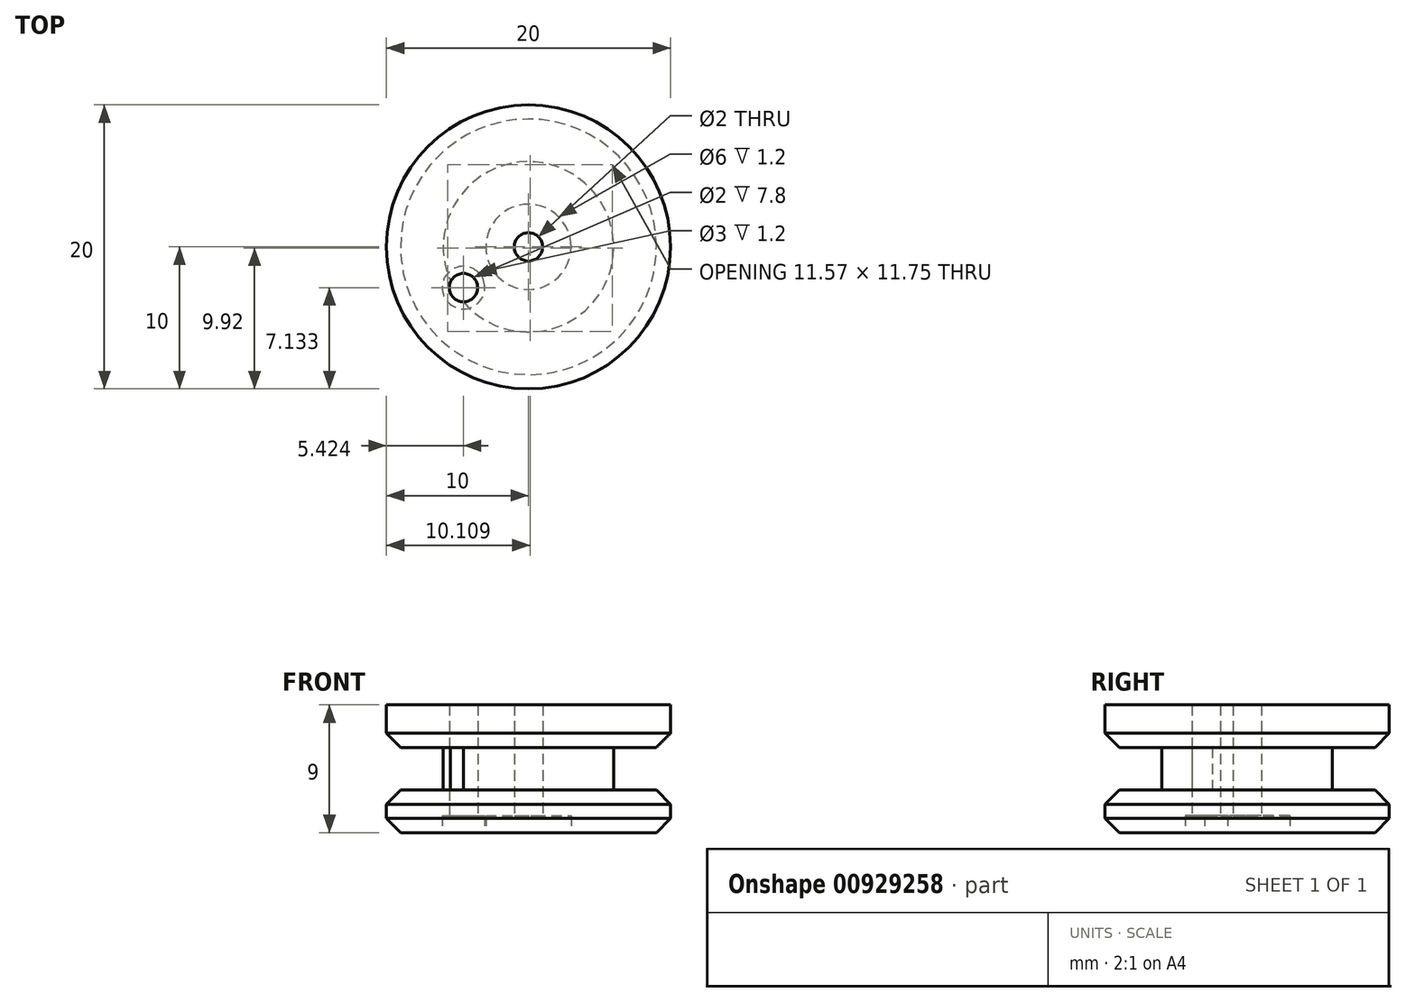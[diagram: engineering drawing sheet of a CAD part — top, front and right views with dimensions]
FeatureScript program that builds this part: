
annotation { "Feature Type Name" : "Feature", "Feature Type Description" : "" }
export const myFeature = defineFeature(function(context is Context, id is Id, definition is map)
    precondition{}
    {
        {
            var Q0;
            Q0=qCreatedBy(makeId("Top.planeOp"),FACE);
            var sketch = newSketch(context, id + "F0", { "sketchPlane" : qUnion([Q0])});
            skCircle(sketch, "E0", {"center": v(0, 0) * mm, "radius": 10 * mm});
            skSolve(sketch);
        }
        {
            var Q0;
            Q0=makeQuery(id+"F0.imprint","IMPRINT",FACE,{"disambiguationData":[TD([[makeQuery(id+"F0.imprint","IMPRINT",EDGE,{"derivedFrom":sQuery(id+"F0.wireOp",EDGE,"E0")}),1.0]])]});
            extrude(context, id + "F1", {"entities" : qUnion([Q0]), "depth" : 3 * mm, "offsetDistance" : 25 * mm});
        }
        {
            var Q0;
            Q0=makeQuery(id+"F0.imprint","IMPRINT",FACE,{"disambiguationData":[TD([[makeQuery(id+"F0.imprint","IMPRINT",EDGE,{"derivedFrom":sQuery(id+"F0.wireOp",EDGE,"E0")}),1.0]])]});
            var sketch = newSketch(context, id + "F2", { "sketchPlane" : qUnion([Q0])});
            skCircle(sketch, "E1", {"center": v(0, 0) * mm, "radius": 6 * mm});
            skSolve(sketch);
        }
        {
            var Q0;
            Q0=makeQuery(id+"F2.imprint","IMPRINT",FACE,{"disambiguationData":[TD([[makeQuery(id+"F2.imprint","IMPRINT",EDGE,{"derivedFrom":sQuery(id+"F2.wireOp",EDGE,"E1")}),1.0]])]});
            extrude(context, id + "F3", {"entities" : qUnion([Q0]), "operationType" : NewBodyOperationType.ADD, "oppositeDirection" : true, "depth" : 3 * mm, "offsetDistance" : 25 * mm});
        }
        {
            var Q0;
            Q0=makeQuery(id+"F3.opExtrude","CAP_FACE",FACE,{"disambiguationData":[OSD([sQuery(id+"F2.wireOp",EDGE,"E1")])],"isStart":false});
            var sketch = newSketch(context, id + "F4", { "sketchPlane" : qUnion([Q0])});
            skCircle(sketch, "E2", {"center": v(0, 0) * mm, "radius": 10 * mm});
            skSolve(sketch);
        }
        {
            var Q0;
            Q0=makeQuery(id+"F4.imprint","IMPRINT",FACE,{"disambiguationData":[TD([[makeQuery(id+"F4.imprint","IMPRINT",EDGE,{"derivedFrom":sQuery(id+"F4.wireOp",EDGE,"E2")}),1.0]])]});
            var Q1;
            Q1=makeQuery(id+"F4.imprint","IMPRINT",FACE,{"disambiguationData":[TD([[makeQuery(id+"F4.imprint","IMPRINT",EDGE,{"derivedFrom":makeQuery(id+"F3.opExtrude","CAP_EDGE",EDGE,{"disambiguationData":[OSD([sQuery(id+"F2.wireOp",EDGE,"E1")])],"isStart":false})}),-1.0]])]});
            extrude(context, id + "F5", {"entities" : qUnion([Q0, Q1]), "operationType" : NewBodyOperationType.ADD, "depth" : 3 * mm, "offsetDistance" : 25 * mm});
        }
        {
            var Q0;
            Q0=makeQuery(id+"F3.opExtrude","CAP_EDGE",EDGE,{"disambiguationData":[OSD([sQuery(id+"F2.wireOp",EDGE,"E1")])],"isStart":true});
            var Q1;
            Q1=makeQuery(id+"F5.opExtrude","CAP_EDGE",EDGE,{"disambiguationData":[OSD([sQuery(id+"F4.wireOp",EDGE,"E2")])],"isStart":true});
            var Q2;
            Q2=makeQuery(id+"F1.opExtrude","CAP_EDGE",EDGE,{"disambiguationData":[OSD([sQuery(id+"F0.wireOp",EDGE,"E0")])],"isStart":true});
            var Q3;
            Q3=makeQuery(id+"F3.opExtrude","CAP_EDGE",EDGE,{"disambiguationData":[OSD([sQuery(id+"F2.wireOp",EDGE,"E1")])],"isStart":false});
            var Q4;
            Q4=makeQuery(id+"F5.opExtrude","CAP_EDGE",EDGE,{"disambiguationData":[OSD([sQuery(id+"F4.wireOp",EDGE,"E2")])],"isStart":false});
            chamfer(context, id + "F6", {"entities" : qUnion([Q0, Q1, Q2, Q3, Q4]), "width" : 1 * mm, "tangentPropagation" : true});
        }
        {
            var Q0;
            Q0=makeQuery(id+"F5.opExtrude","CAP_FACE",FACE,{"disambiguationData":[OSD([sQuery(id+"F4.wireOp",EDGE,"E2")])],"isStart":false});
            var sketch = newSketch(context, id + "F7", { "sketchPlane" : qUnion([Q0])});
            skPoint(sketch, "E3.0", {"position": v(0, 0) * mm});
            skSolve(sketch);
        }
        {
            var Q0;
            Q0=sQuery(id+"F7.wireOp",VERTEX,"E3.0");
            var Q1;
            Q1=makeQuery(id+"F1.opExtrude","SWEPT_BODY",BODY,{"disambiguationData":[OSD([sQuery(id+"F0.wireOp",EDGE,"E0")])]});
            hole(context, id + "F8", {"style" : HoleStyle.C_BORE, "endStyle" : HoleEndStyle.BLIND, "holeDiameter" : 2 * mm, "cBoreDiameter" : 6 * mm, "cBoreDepth" : 1.2 * mm, "majorDiameter" : 5 * mm, "holeDepth" : 27 * mm, "tappedDepth" : 12 * mm, "tapClearance" : 3, "startFromSketch" : true, "locations" : qUnion([Q0]), "scope" : qUnion([Q1])});
        }
        {
            var Q0;
            Q0=makeQuery(id+"F5.opExtrude","CAP_FACE",FACE,{"disambiguationData":[OSD([sQuery(id+"F4.wireOp",EDGE,"E2")])],"isStart":false});
            var sketch = newSketch(context, id + "F9", { "sketchPlane" : qUnion([Q0])});
            skPoint(sketch, "E4", {"position": v(-4.58, 2.87) * mm});
            skCircle(sketch, "E5.0", {"center": v(0, 0) * mm, "radius": 6 * mm});
            skSolve(sketch);
        }
        {
            var Q0;
            Q0=sQuery(id+"F9.wireOp",VERTEX,"E4");
            var Q1;
            Q1=makeQuery(id+"F1.opExtrude","SWEPT_BODY",BODY,{"disambiguationData":[OSD([sQuery(id+"F0.wireOp",EDGE,"E0")])]});
            hole(context, id + "F10", {"style" : HoleStyle.C_BORE, "endStyle" : HoleEndStyle.BLIND, "holeDiameter" : 2 * mm, "cBoreDiameter" : 3 * mm, "cBoreDepth" : 1.2 * mm, "majorDiameter" : 5 * mm, "holeDepth" : 9 * mm, "tappedDepth" : 12 * mm, "tapClearance" : 3, "startFromSketch" : true, "locations" : qUnion([Q0]), "scope" : qUnion([Q1])});
        }
    });
